# Revit family: Screen-Leg_Mounted-Teknion-JNSEEL-Felt_Elevated-R2015
name_source: partatom
category: Furniture
revit_build: Autodesk Revit Architecture 2015 (Build: 20140323_1530(x64)
units: mm (PartAtom-declared; Revit-internal decimal feet)

## types (3) — shared parameters
Assembly Code = E2020200
Description = Felt Elevated Screen – Leg-Mounted
Manufacturer = Teknion
Manufacturer Fax = 416.661.4586
Part Number = JNSEEL
Product Documentation Link = http://www.teknion.com
Product Line = Expansion Cityline
Product Page URL = http://www.teknion.com
Series = Expansion Cityline
Sustainability Data = http://www.teknion.com
URL = www.teknion.com
Unit Weight URL = http://www.teknion.com
Warranty = http://www.teknion.com

## per-type parameters (varying)
| type | Model |
| Double-Sided Leg Overlay | JNSEELD |
| Left Configuration | JNSEELL |
| Right Configuration | JNSEELR |

type visibility flags: 3 boolean params named "<type name>" — each type sets only its own to Yes (folded from table)

## geometry (parser evidence)
native form markers: Blend x2, Sweep x2
no freeform markers — native parametric forms only
